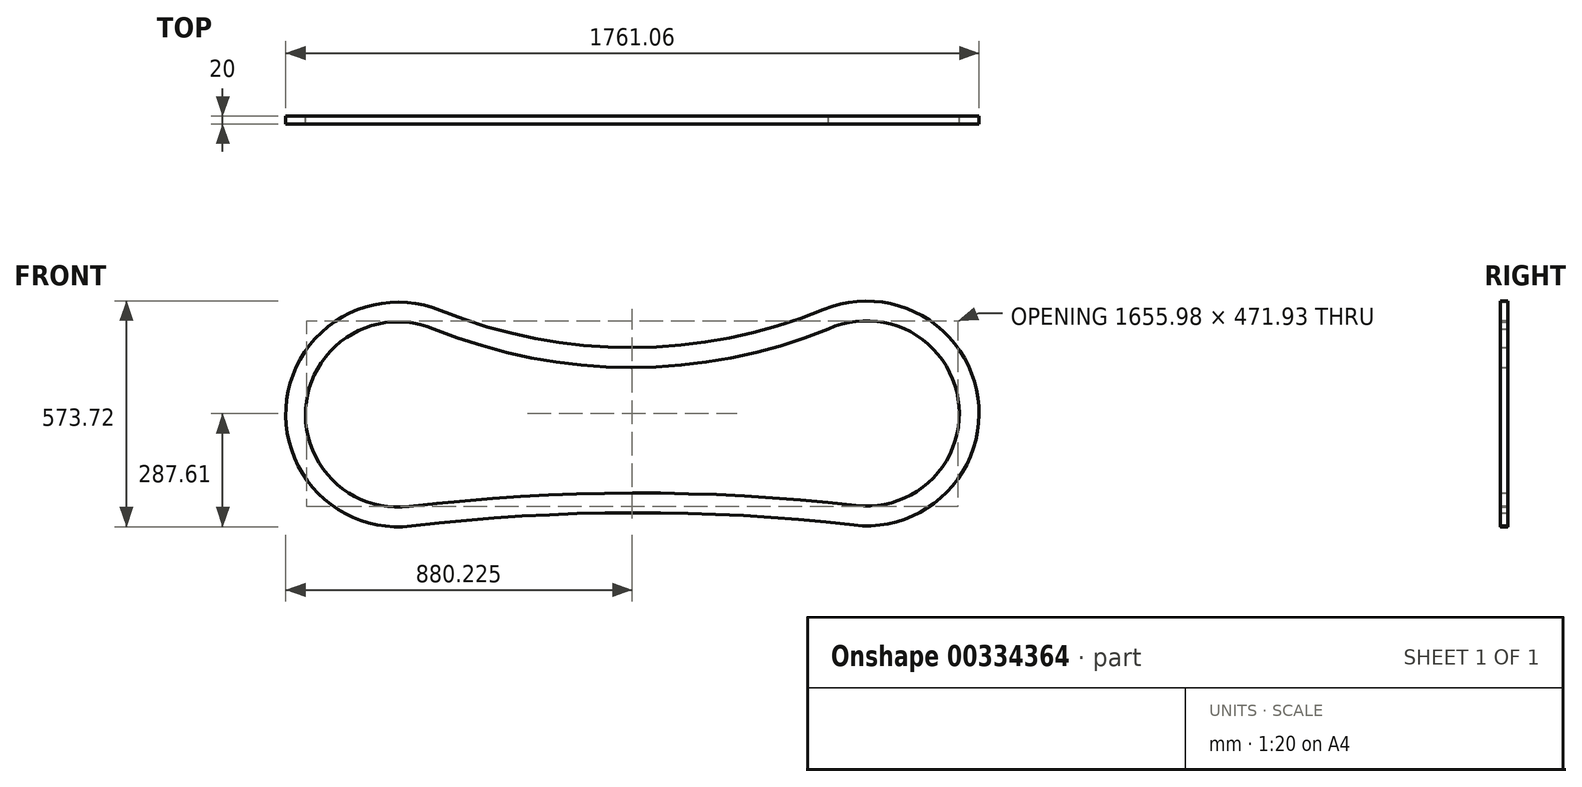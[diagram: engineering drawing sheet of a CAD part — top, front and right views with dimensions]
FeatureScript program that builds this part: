
annotation { "Feature Type Name" : "Feature", "Feature Type Description" : "" }
export const myFeature = defineFeature(function(context is Context, id is Id, definition is map)
    precondition{}
    {
        {
            var Q0;
            Q0=qCreatedBy(makeId("Front.planeOp"),FACE);
            var sketch = newSketch(context, id + "F0", { "sketchPlane" : qUnion([Q0])});
            skPoint(sketch, "E0.endSnap0", {"position": v(-2.6, 0) * mm});
            skArc(sketch, "E1", {"start": v(548.56, -281.03) * mm, "mid": v(-13.43, -249.62) * mm, "end": v(-575.28, -283.54) * mm});
            skArc(sketch, "E2", {"start": v(-501.27, 264.43) * mm, "mid": v(-14.37, 169.63) * mm, "end": v(472.1, 266.6) * mm});
            skArc(sketch, "E3", {"start": v(-501.27, 264.43) * mm, "mid": v(-891.96, 38.22) * mm, "end": v(-575.28, -283.54) * mm});
            skArc(sketch, "E4", {"start": v(548.56, -281.03) * mm, "mid": v(863.8, 42.14) * mm, "end": v(472.1, 266.6) * mm});
            skArc(sketch, "E5.0", {"start": v(-518.47, 217.44) * mm, "mid": v(-842.28, 32.41) * mm, "end": v(-581.18, -233.89) * mm});
            skArc(sketch, "E6.0", {"start": v(-518.47, 217.44) * mm, "mid": v(8.21, 119.84) * mm, "end": v(530.82, 237.3) * mm});
            skArc(sketch, "E7.0", {"start": v(554.24, -231.35) * mm, "mid": v(813.7, 39.17) * mm, "end": v(483.85, 217.22) * mm});
            skArc(sketch, "E8.0", {"start": v(554.24, -231.35) * mm, "mid": v(-13.54, -199.62) * mm, "end": v(-581.18, -233.89) * mm});
            skLineSegment(sketch, "E9", {"start": v(581, 2.66) * mm, "end": v(-609, 0) * mm});
            skSolve(sketch);
        }
        {
            var Q0;
            Q0=makeQuery(id+"F0.imprint","IMPRINT",FACE,{"disambiguationData":[TD([[makeQuery(id+"F0.imprint","IMPRINT",EDGE,{"derivedFrom":sQuery(id+"F0.wireOp",EDGE,"E1")}),-1.0]])]});
            extrude(context, id + "F1", {"entities" : qUnion([Q0]), "depth" : 20 * mm});
        }
    });
